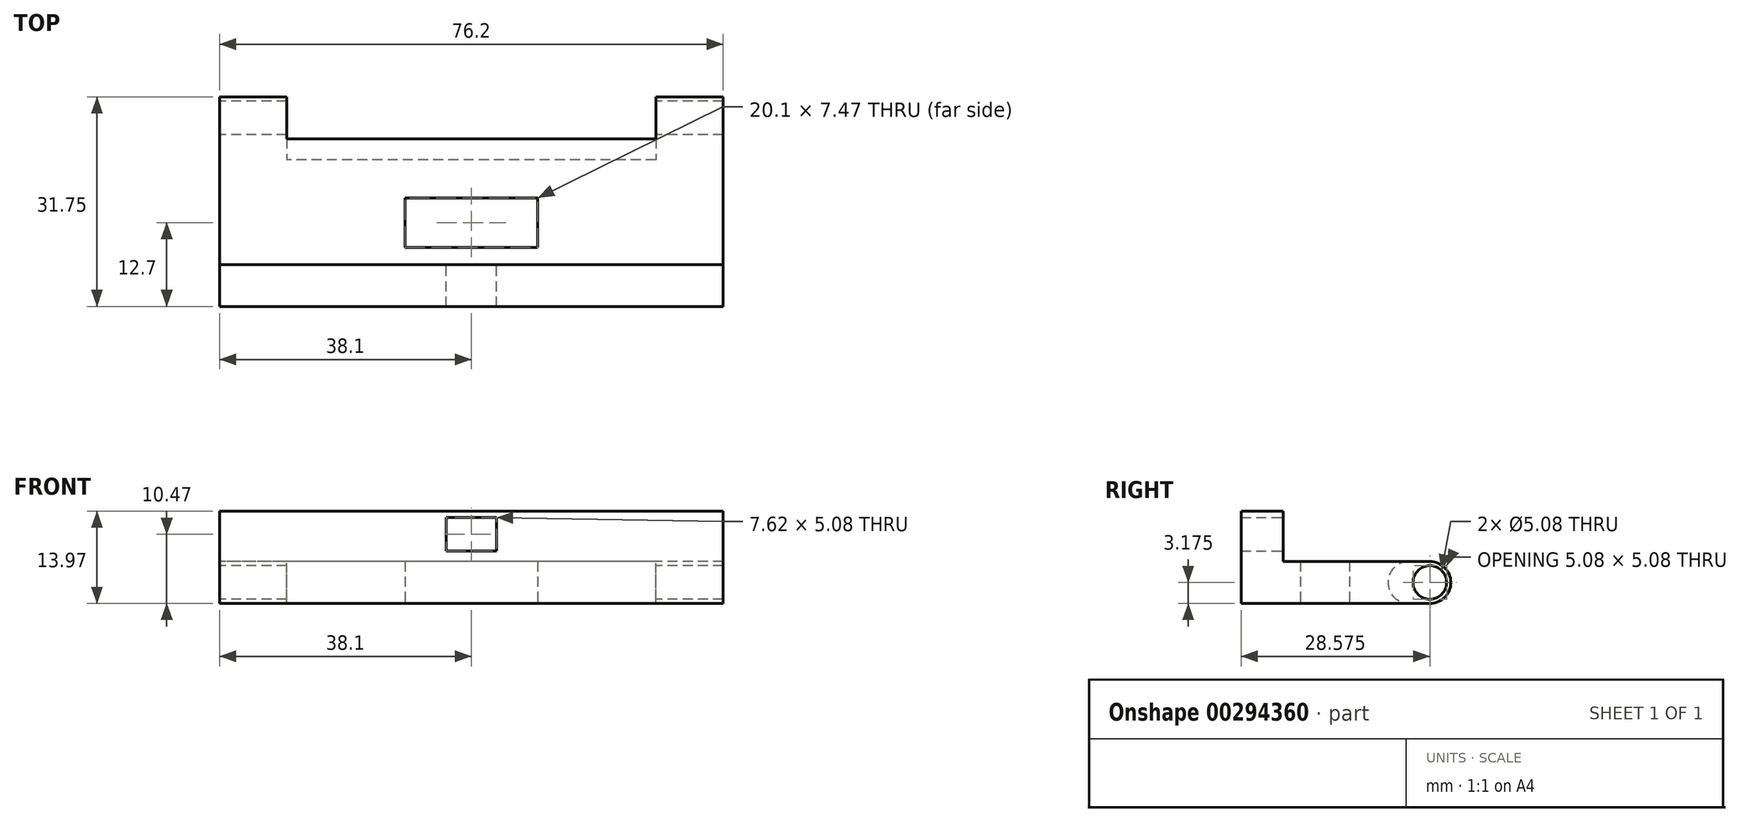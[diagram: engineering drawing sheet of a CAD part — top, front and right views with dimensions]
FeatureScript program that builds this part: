
annotation { "Feature Type Name" : "Feature", "Feature Type Description" : "" }
export const myFeature = defineFeature(function(context is Context, id is Id, definition is map)
    precondition{}
    {
        {
            var Q0;
            Q0=qCreatedBy(makeId("Top.planeOp"),FACE);
            var sketch = newSketch(context, id + "F0", { "sketchPlane" : qUnion([Q0])});
            skLineSegment(sketch, "E0.bottom", {"start": v(38.1, -12.7) * mm, "end": v(-38.1, -12.7) * mm});
            skLineSegment(sketch, "E0.top", {"start": v(38.1, 12.7) * mm, "end": v(-38.1, 12.7) * mm});
            skLineSegment(sketch, "E0.left", {"start": v(38.1, -12.7) * mm, "end": v(38.1, 12.7) * mm});
            skLineSegment(sketch, "E0.right", {"start": v(-38.1, -12.7) * mm, "end": v(-38.1, 12.7) * mm});
            skPoint(sketch, "E0.middle", {"position": v(0, 0) * mm});
            skSolve(sketch);
        }
        {
            var Q0;
            Q0=qCreatedBy(makeId("Top.planeOp"),FACE);
            var sketch = newSketch(context, id + "F1", { "sketchPlane" : qUnion([Q0])});
            skLineSegment(sketch, "E1.bottom", {"start": v(10.05, -3.74) * mm, "end": v(-10.05, -3.74) * mm});
            skLineSegment(sketch, "E1.top", {"start": v(10.05, 3.74) * mm, "end": v(-10.05, 3.74) * mm});
            skLineSegment(sketch, "E1.left", {"start": v(10.05, -3.74) * mm, "end": v(10.05, 3.74) * mm});
            skLineSegment(sketch, "E1.right", {"start": v(-10.05, -3.74) * mm, "end": v(-10.05, 3.74) * mm});
            skPoint(sketch, "E1.middle", {"position": v(0, 0) * mm});
            skSolve(sketch);
        }
        {
            var Q0;
            Q0=makeQuery(id+"F0.imprint","IMPRINT",FACE,{"disambiguationData":[TD([[makeQuery(id+"F0.imprint","IMPRINT",EDGE,{"derivedFrom":sQuery(id+"F0.wireOp",EDGE,"E0.bottom")}),-1.0]])]});
            extrude(context, id + "F2", {"entities" : qUnion([Q0]), "depth" : 6.35 * mm});
        }
        {
            var Q0;
            Q0 = qSketchRegion(id + "F1", true);
            extrude(context, id + "F3", {"entities" : qUnion([Q0]), "operationType" : NewBodyOperationType.REMOVE, "depth" : 6.35 * mm});
        }
        {
            var Q0;
            Q0=qCreatedBy(makeId("Front.planeOp"),FACE);
            var sketch = newSketch(context, id + "F4", { "sketchPlane" : qUnion([Q0])});
            skLineSegment(sketch, "E2.bottom", {"start": v(38.1, 0) * mm, "end": v(27.94, 0) * mm});
            skLineSegment(sketch, "E2.top", {"start": v(38.1, 6.35) * mm, "end": v(27.94, 6.35) * mm});
            skLineSegment(sketch, "E2.left", {"start": v(38.1, 0) * mm, "end": v(38.1, 6.35) * mm});
            skLineSegment(sketch, "E2.right", {"start": v(27.94, 0) * mm, "end": v(27.94, 6.35) * mm});
            skLineSegment(sketch, "E3.MirrorCS", {"start": v(-27.94, 0) * mm, "end": v(-27.94, 6.35) * mm});
            skLineSegment(sketch, "E4.MirrorCS", {"start": v(-38.1, 0) * mm, "end": v(-38.1, 6.35) * mm});
            skLineSegment(sketch, "E5.MirrorCS", {"start": v(-38.1, 6.35) * mm, "end": v(-27.94, 6.35) * mm});
            skLineSegment(sketch, "E6.MirrorCS", {"start": v(-38.1, 0) * mm, "end": v(-27.94, 0) * mm});
            skSolve(sketch);
        }
        {
            var Q0;
            Q0 = qSketchRegion(id + "F4", true);
            extrude(context, id + "F5", {"entities" : qUnion([Q0]), "operationType" : NewBodyOperationType.ADD, "oppositeDirection" : true, "depth" : 19.05 * mm});
        }
        {
            var Q0;
            Q0=makeQuery(id+"F5.boolean.opBoolean","MERGE",FACE,{"derivedFrom":[makeQuery(id+"F2.opExtrude","SWEPT_FACE",FACE,{"disambiguationData":[OSD([sQuery(id+"F0.wireOp",EDGE,"E0.right")])]}),makeQuery(id+"F5.opExtrude","SWEPT_FACE",FACE,{"disambiguationData":[OSD([sQuery(id+"F4.wireOp",EDGE,"E4.MirrorCS")])]})]});
            var sketch = newSketch(context, id + "F6", { "sketchPlane" : qUnion([Q0])});
            skCircle(sketch, "E7", {"center": v(-15.87, 3.17) * mm, "radius": 2.54 * mm});
            skPoint(sketch, "E8", {"position": v(-19.05, 3.17) * mm});
            skCircle(sketch, "E9", {"center": v(-15.87, 3.17) * mm, "radius": 3.18 * mm});
            skSolve(sketch);
        }
        {
            var Q0;
            Q0=makeQuery(id+"F6.imprint","IMPRINT",FACE,{"disambiguationData":[TD([[makeQuery(id+"F6.imprint","IMPRINT",EDGE,{"derivedFrom":sQuery(id+"F6.wireOp",EDGE,"E7")}),1.0]])]});
            extrude(context, id + "F7", {"entities" : qUnion([Q0]), "operationType" : NewBodyOperationType.REMOVE, "oppositeDirection" : true, "depth" : 76.2 * mm});
        }
        {
            var Q0;
            {var subQ0=sQuery(id+"F6.wireOp",EDGE,"E9");var subQ1=sQuery(id+"F4.wireOp",EDGE,"E4.MirrorCS");var subQ2=makeQuery(id+"F5.opExtrude","CAP_EDGE",EDGE,{"disambiguationData":[OSD([subQ1])],"isStart":false});var subQ3=makeQuery(id+"F6.imprint","INTERSECT",VERTEX,{"derivedFrom":[subQ2,subQ0]});Q0=makeQuery(id+"F6.imprint","IMPRINT",FACE,{"disambiguationData":[TD([[makeQuery(id+"F6.imprint","IMPRINT",EDGE,{"disambiguationData":[TD([[subQ3,-1.0]])],"derivedFrom":subQ0}),-1.0]])]});}
            var Q1;
            {var subQ0=sQuery(id+"F6.wireOp",EDGE,"E9");var subQ1=sQuery(id+"F4.wireOp",EDGE,"E4.MirrorCS");var subQ2=makeQuery(id+"F5.opExtrude","CAP_EDGE",EDGE,{"disambiguationData":[OSD([subQ1])],"isStart":false});var subQ3=makeQuery(id+"F6.imprint","INTERSECT",VERTEX,{"derivedFrom":[subQ2,subQ0]});Q1=makeQuery(id+"F6.imprint","IMPRINT",FACE,{"disambiguationData":[TD([[makeQuery(id+"F6.imprint","IMPRINT",EDGE,{"disambiguationData":[TD([[subQ3,1.0]])],"derivedFrom":subQ0}),-1.0]])]});}
            extrude(context, id + "F8", {"entities" : qUnion([Q0, Q1]), "operationType" : NewBodyOperationType.REMOVE, "oppositeDirection" : true, "depth" : 76.2 * mm});
        }
        {
            var Q0;
            Q0=qCreatedBy(makeId("Right.planeOp"),FACE);
            var sketch = newSketch(context, id + "F9", { "sketchPlane" : qUnion([Q0])});
            skLineSegment(sketch, "E10", {"start": v(12.7, 0) * mm, "end": v(12.7, 6.35) * mm});
            skArc(sketch, "E11", {"start": v(12.7, 6.35) * mm, "mid": v(9.53, 3.18) * mm, "end": v(12.7, 0) * mm});
            skSolve(sketch);
        }
        {
            var Q0;
            Q0 = qSketchRegion(id + "F9", true);
            extrude(context, id + "F10", {"entities" : qUnion([Q0]), "operationType" : NewBodyOperationType.REMOVE, "endBound" : BoundingType.SYMMETRIC, "depth" : 55.88 * mm});
        }
        {
            var Q0;
            Q0=qCreatedBy(makeId("Top.planeOp"),FACE);
            var sketch = newSketch(context, id + "F11", { "sketchPlane" : qUnion([Q0])});
            skLineSegment(sketch, "E12.bottom", {"start": v(-38.1, -12.7) * mm, "end": v(38.1, -12.7) * mm});
            skLineSegment(sketch, "E12.top", {"start": v(-38.1, -6.35) * mm, "end": v(38.1, -6.35) * mm});
            skLineSegment(sketch, "E12.left", {"start": v(-38.1, -12.7) * mm, "end": v(-38.1, -6.35) * mm});
            skLineSegment(sketch, "E12.right", {"start": v(38.1, -12.7) * mm, "end": v(38.1, -6.35) * mm});
            skSolve(sketch);
        }
        {
            var Q0;
            Q0 = qSketchRegion(id + "F11", true);
            extrude(context, id + "F12", {"entities" : qUnion([Q0]), "operationType" : NewBodyOperationType.ADD, "depth" : 13.97 * mm});
        }
        {
            var Q0;
            Q0=makeQuery(id+"F12.boolean.opBoolean","MERGE",FACE,{"derivedFrom":[makeQuery(id+"F2.opExtrude","SWEPT_FACE",FACE,{"disambiguationData":[OSD([sQuery(id+"F0.wireOp",EDGE,"E0.bottom")])]}),makeQuery(id+"F12.opExtrude","SWEPT_FACE",FACE,{"disambiguationData":[OSD([sQuery(id+"F11.wireOp",EDGE,"E12.bottom")])]})]});
            var sketch = newSketch(context, id + "F13", { "sketchPlane" : qUnion([Q0])});
            skLineSegment(sketch, "E13.right", {"start": v(55.82, 5.12) * mm, "end": v(55.82, 5.12) * mm});
            skLineSegment(sketch, "E14.bottom", {"start": v(-3.81, 7.93) * mm, "end": v(3.81, 7.93) * mm});
            skLineSegment(sketch, "E14.top", {"start": v(-3.81, 13.01) * mm, "end": v(3.8, 13.01) * mm});
            skLineSegment(sketch, "E14.left", {"start": v(-3.81, 7.93) * mm, "end": v(-3.81, 13.01) * mm});
            skLineSegment(sketch, "E14.right", {"start": v(3.81, 7.93) * mm, "end": v(3.8, 13.01) * mm});
            skPoint(sketch, "E14.middle", {"position": v(0, 10.47) * mm});
            skSolve(sketch);
        }
        {
            var Q0;
            Q0 = qSketchRegion(id + "F13", true);
            extrude(context, id + "F14", {"entities" : qUnion([Q0]), "operationType" : NewBodyOperationType.ADD, "depth" : 25.4 * mm});
        }
        {
            var Q0;
            Q0=makeQuery(id+"F14.opExtrude","CAP_FACE",FACE,{"disambiguationData":[OSD([sQuery(id+"F13.wireOp",EDGE,"E14.bottom"),sQuery(id+"F13.wireOp",EDGE,"E14.top"),sQuery(id+"F13.wireOp",EDGE,"E14.left"),sQuery(id+"F13.wireOp",EDGE,"E14.right")])],"isStart":false});
            extrude(context, id + "F15", {"entities" : qUnion([Q0]), "operationType" : NewBodyOperationType.REMOVE, "endBound" : BoundingType.SYMMETRIC, "depth" : 381 * mm});
        }
    });
